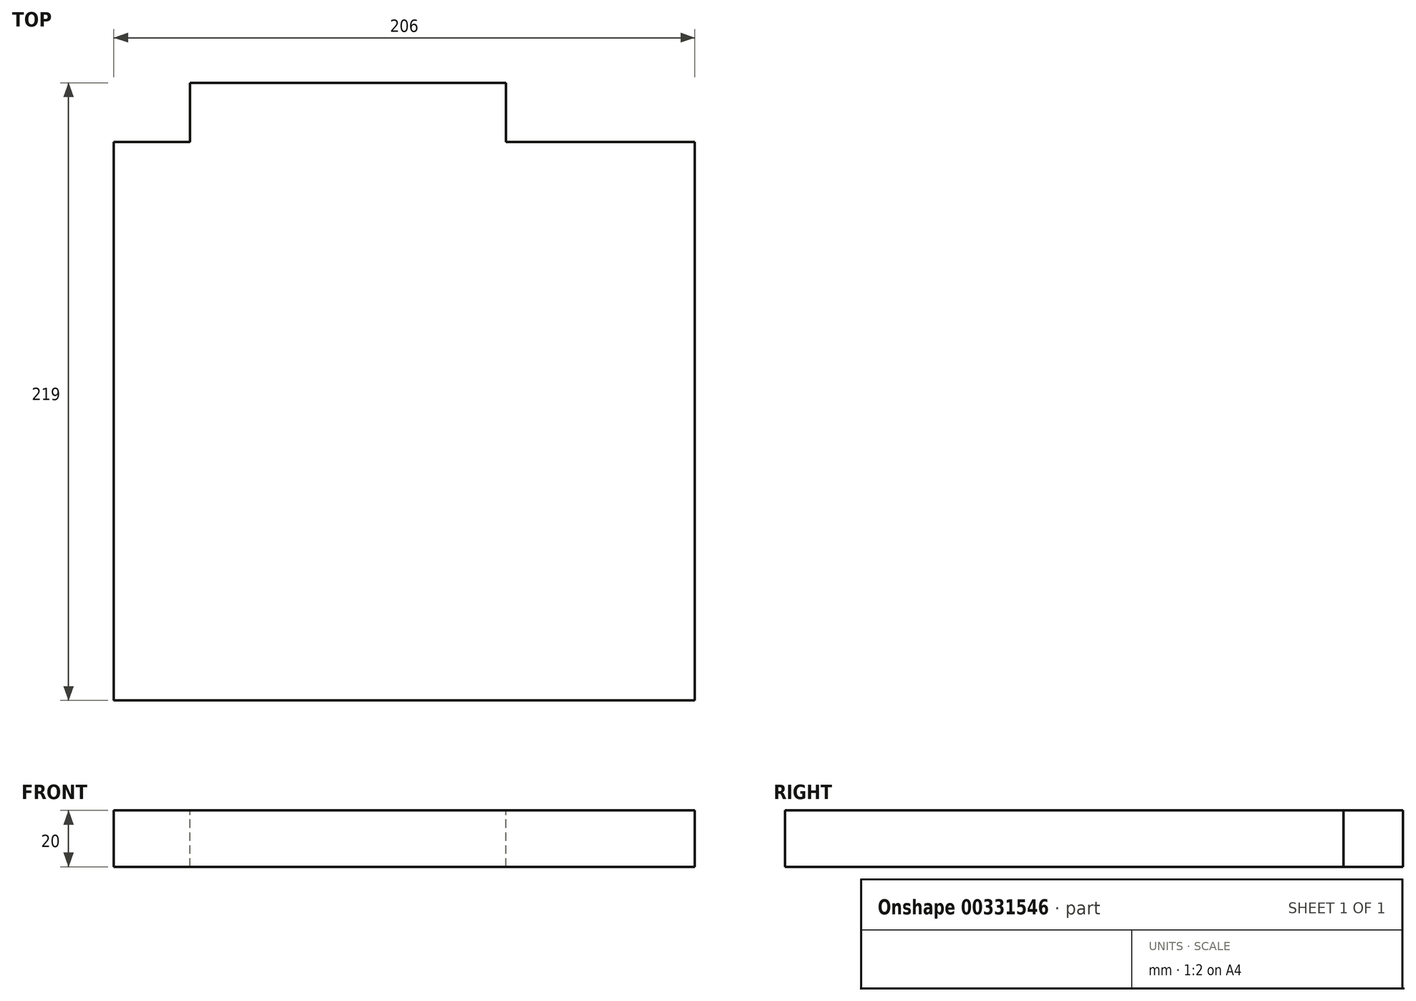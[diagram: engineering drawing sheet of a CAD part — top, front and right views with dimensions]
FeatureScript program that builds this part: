
annotation { "Feature Type Name" : "Feature", "Feature Type Description" : "" }
export const myFeature = defineFeature(function(context is Context, id is Id, definition is map)
    precondition{}
    {
        {
            var Q0;
            Q0=qCreatedBy(makeId("Top.planeOp"),FACE);
            var sketch = newSketch(context, id + "F0", { "sketchPlane" : qUnion([Q0])});
            skLineSegment(sketch, "E0", {"start": v(1313, 440) * mm, "end": v(1313, 406) * mm});
            skLineSegment(sketch, "E1", {"start": v(1313, -267) * mm, "end": v(1313, -301) * mm});
            skLineSegment(sketch, "E2", {"start": v(1313, -301) * mm, "end": v(647, -301) * mm});
            skLineSegment(sketch, "E3", {"start": v(1279, -267) * mm, "end": v(647, -267) * mm});
            skLineSegment(sketch, "E4", {"start": v(1279, 406) * mm, "end": v(688, 406) * mm});
            skLineSegment(sketch, "E5", {"start": v(688, 406) * mm, "end": v(688, -75) * mm});
            skLineSegment(sketch, "E6", {"start": v(688, -75) * mm, "end": v(413, -75) * mm});
            skLineSegment(sketch, "E7", {"start": v(647, -301) * mm, "end": v(647, -267) * mm});
            skLineSegment(sketch, "E8", {"start": v(536, -301) * mm, "end": v(536, -267) * mm});
            skLineSegment(sketch, "E9", {"start": v(536, -267) * mm, "end": v(328, -267) * mm});
            skLineSegment(sketch, "E10", {"start": v(328, -267) * mm, "end": v(328, -407) * mm});
            skLineSegment(sketch, "E11", {"start": v(328, -407) * mm, "end": v(-40, -407) * mm});
            skLineSegment(sketch, "E12", {"start": v(-40, -407) * mm, "end": v(-40, -188) * mm});
            skLineSegment(sketch, "E13", {"start": v(-40, -188) * mm, "end": v(-105, -188) * mm});
            skLineSegment(sketch, "E14", {"start": v(536, -301) * mm, "end": v(362, -301) * mm});
            skLineSegment(sketch, "E15", {"start": v(362, -301) * mm, "end": v(362, -440) * mm});
            skLineSegment(sketch, "E16", {"start": v(-60, -407) * mm, "end": v(-60, -215) * mm});
            skLineSegment(sketch, "E17", {"start": v(-60, -215) * mm, "end": v(-105, -215) * mm});
            skLineSegment(sketch, "E18", {"start": v(-105, -188) * mm, "end": v(-105, -215) * mm});
            skLineSegment(sketch, "E19", {"start": v(-60, -407) * mm, "end": v(-282, -407) * mm});
            skLineSegment(sketch, "E20", {"start": v(-282, -407) * mm, "end": v(-282, -287) * mm});
            skLineSegment(sketch, "E21", {"start": v(-282, -287) * mm, "end": v(-330, -287) * mm});
            skLineSegment(sketch, "E22", {"start": v(-330, -287) * mm, "end": v(-330, -407) * mm});
            skLineSegment(sketch, "E23", {"start": v(-330, -407) * mm, "end": v(-497, -407) * mm});
            skLineSegment(sketch, "E24", {"start": v(-197, -188) * mm, "end": v(-197, -215) * mm});
            skLineSegment(sketch, "E25", {"start": v(-197, -188) * mm, "end": v(-765, -188) * mm});
            skLineSegment(sketch, "E26", {"start": v(-197, -215) * mm, "end": v(-497, -215) * mm});
            skLineSegment(sketch, "E27", {"start": v(-497, -215) * mm, "end": v(-497, -231) * mm});
            skLineSegment(sketch, "E28", {"start": v(-497, -231) * mm, "end": v(-497, -293) * mm});
            skLineSegment(sketch, "E29", {"start": v(-497, -407) * mm, "end": v(-497, -349) * mm});
            skLineSegment(sketch, "E30", {"start": v(413, -75) * mm, "end": v(413, -54) * mm});
            skLineSegment(sketch, "E31", {"start": v(413, -54) * mm, "end": v(667, -54) * mm});
            skLineSegment(sketch, "E32", {"start": v(667, -54) * mm, "end": v(667, 406) * mm});
            skLineSegment(sketch, "E33", {"start": v(667, 406) * mm, "end": v(495, 406) * mm});
            skLineSegment(sketch, "E34", {"start": v(312, 406) * mm, "end": v(391, 406) * mm});
            skLineSegment(sketch, "E35", {"start": v(391, 406) * mm, "end": v(391, 440) * mm});
            skLineSegment(sketch, "E36", {"start": v(495, 406) * mm, "end": v(495, 440) * mm});
            skLineSegment(sketch, "E37", {"start": v(1313, 440) * mm, "end": v(495, 440) * mm});
            skLineSegment(sketch, "E38", {"start": v(312, -75) * mm, "end": v(60, -75) * mm});
            skLineSegment(sketch, "E39", {"start": v(-1279, 406) * mm, "end": v(-1279, 7) * mm});
            skLineSegment(sketch, "E40", {"start": v(-790, 406) * mm, "end": v(-790, 7) * mm});
            skLineSegment(sketch, "E41", {"start": v(-1279, 7) * mm, "end": v(-910, 7) * mm});
            skLineSegment(sketch, "E42", {"start": v(-790, 7) * mm, "end": v(-808, 7) * mm});
            skLineSegment(sketch, "E43", {"start": v(-765, -188) * mm, "end": v(-765, -208) * mm});
            skLineSegment(sketch, "E44", {"start": v(290, 141) * mm, "end": v(290, 406) * mm});
            skLineSegment(sketch, "E45", {"start": v(290, 141) * mm, "end": v(75, 141) * mm});
            skLineSegment(sketch, "E46", {"start": v(75, -46) * mm, "end": v(75, 141) * mm});
            skLineSegment(sketch, "E47", {"start": v(60, -75) * mm, "end": v(60, -46) * mm});
            skLineSegment(sketch, "E48", {"start": v(391, 406) * mm, "end": v(312, 406) * mm});
            skLineSegment(sketch, "E49", {"start": v(-139, 406) * mm, "end": v(-139, 440) * mm});
            skLineSegment(sketch, "E50", {"start": v(-318, 406) * mm, "end": v(-318, 440) * mm});
            skLineSegment(sketch, "E51", {"start": v(-515, 406) * mm, "end": v(-515, 440) * mm});
            skLineSegment(sketch, "E52", {"start": v(-694, 406) * mm, "end": v(-694, 440) * mm});
            skLineSegment(sketch, "E53", {"start": v(-770, 406) * mm, "end": v(-770, 9) * mm});
            skLineSegment(sketch, "E54", {"start": v(-694, 406) * mm, "end": v(-770, 406) * mm});
            skLineSegment(sketch, "E55", {"start": v(75, 406) * mm, "end": v(-139, 406) * mm});
            skLineSegment(sketch, "E56", {"start": v(-318, 406) * mm, "end": v(-515, 406) * mm});
            skLineSegment(sketch, "E57", {"start": v(-318, 440) * mm, "end": v(-515, 440) * mm});
            skLineSegment(sketch, "E58", {"start": v(-770, 9) * mm, "end": v(-754, 9) * mm});
            skLineSegment(sketch, "E59", {"start": v(-677, 9) * mm, "end": v(-659, 9) * mm});
            skLineSegment(sketch, "E60", {"start": v(-659, 9) * mm, "end": v(-659, -5) * mm});
            skLineSegment(sketch, "E61", {"start": v(-659, -5) * mm, "end": v(-659, -46) * mm});
            skLineSegment(sketch, "E62", {"start": v(-659, -46) * mm, "end": v(-60, -46) * mm});
            skLineSegment(sketch, "E63", {"start": v(-60, -75) * mm, "end": v(-60, -46) * mm});
            skLineSegment(sketch, "E64", {"start": v(60, -75) * mm, "end": v(128, -75) * mm});
            skLineSegment(sketch, "E65", {"start": v(60, -46) * mm, "end": v(75, -46) * mm});
            skLineSegment(sketch, "E66", {"start": v(96, -46) * mm, "end": v(290, -46) * mm});
            skLineSegment(sketch, "E67", {"start": v(-60, -75) * mm, "end": v(-677, -75) * mm});
            skLineSegment(sketch, "E68", {"start": v(-677, 9) * mm, "end": v(-677, -75) * mm});
            skLineSegment(sketch, "E69", {"start": v(-754, 9) * mm, "end": v(-754, -13) * mm});
            skLineSegment(sketch, "E70", {"start": v(-808, 7) * mm, "end": v(-808, -13) * mm});
            skLineSegment(sketch, "E71", {"start": v(-808, -13) * mm, "end": v(-754, -13) * mm});
            skLineSegment(sketch, "E72", {"start": v(-910, 7) * mm, "end": v(-910, -29) * mm});
            skLineSegment(sketch, "E73", {"start": v(-1279, -406) * mm, "end": v(-935, -406) * mm});
            skLineSegment(sketch, "E74", {"start": v(-1313, -440) * mm, "end": v(-935, -440) * mm});
            skLineSegment(sketch, "E75", {"start": v(-910, -29) * mm, "end": v(-935, -29) * mm});
            skLineSegment(sketch, "E76", {"start": v(-935, -13) * mm, "end": v(-1279, -13) * mm});
            skLineSegment(sketch, "E77", {"start": v(-910, -132) * mm, "end": v(-935, -132) * mm});
            skLineSegment(sketch, "E78", {"start": v(-910, -29) * mm, "end": v(-910, -13) * mm});
            skLineSegment(sketch, "E79", {"start": v(-935, -406) * mm, "end": v(-935, -132) * mm});
            skLineSegment(sketch, "E80", {"start": v(-935, -29) * mm, "end": v(-935, -13) * mm});
            skLineSegment(sketch, "E81", {"start": v(-877, -208) * mm, "end": v(-877, -188) * mm});
            skLineSegment(sketch, "E82", {"start": v(-910, -132) * mm, "end": v(-910, -188) * mm});
            skLineSegment(sketch, "E83", {"start": v(-877, -188) * mm, "end": v(-910, -188) * mm});
            skLineSegment(sketch, "E84", {"start": v(-877, -208) * mm, "end": v(-904, -208) * mm});
            skLineSegment(sketch, "E85", {"start": v(-904, -208) * mm, "end": v(-904, -406) * mm});
            skLineSegment(sketch, "E86", {"start": v(-904, -406) * mm, "end": v(-648, -406) * mm});
            skLineSegment(sketch, "E87", {"start": v(-765, -208) * mm, "end": v(-648, -208) * mm});
            skLineSegment(sketch, "E88", {"start": v(-648, -208) * mm, "end": v(-648, -273) * mm});
            skLineSegment(sketch, "E89", {"start": v(-648, -406) * mm, "end": v(-648, -343) * mm});
            skLineSegment(sketch, "E90", {"start": v(-935, -440) * mm, "end": v(362, -440) * mm});
            skLineSegment(sketch, "E91", {"start": v(151, 406) * mm, "end": v(151, 440) * mm});
            skLineSegment(sketch, "E92", {"start": v(224, 406) * mm, "end": v(224, 440) * mm});
            skLineSegment(sketch, "E93", {"start": v(290, 406) * mm, "end": v(224, 406) * mm});
            skLineSegment(sketch, "E94", {"start": v(151, 406) * mm, "end": v(96, 406) * mm});
            skLineSegment(sketch, "E95", {"start": v(391, 440) * mm, "end": v(224, 440) * mm});
            skLineSegment(sketch, "E96", {"start": v(151, 440) * mm, "end": v(-139, 440) * mm});
            skLineSegment(sketch, "E97", {"start": v(-907, 406) * mm, "end": v(-907, 440) * mm});
            skLineSegment(sketch, "E98", {"start": v(-1085, 406) * mm, "end": v(-1085, 440) * mm});
            skLineSegment(sketch, "E99", {"start": v(-790, 406) * mm, "end": v(-907, 406) * mm});
            skLineSegment(sketch, "E100", {"start": v(-1085, 406) * mm, "end": v(-1279, 406) * mm});
            skLineSegment(sketch, "E101", {"start": v(-694, 440) * mm, "end": v(-907, 440) * mm});
            skLineSegment(sketch, "E102", {"start": v(-1085, 440) * mm, "end": v(-1313, 440) * mm});
            skLineSegment(sketch, "E103", {"start": v(-1279, -118) * mm, "end": v(-1313, -118) * mm});
            skLineSegment(sketch, "E104", {"start": v(-1279, -297) * mm, "end": v(-1313, -297) * mm});
            skLineSegment(sketch, "E105", {"start": v(-1279, -13) * mm, "end": v(-1279, -118) * mm});
            skLineSegment(sketch, "E106", {"start": v(-1279, -297) * mm, "end": v(-1279, -406) * mm});
            skLineSegment(sketch, "E107", {"start": v(-1313, 440) * mm, "end": v(-1313, -118) * mm});
            skLineSegment(sketch, "E108", {"start": v(-1313, -297) * mm, "end": v(-1313, -440) * mm});
            skLineSegment(sketch, "E109", {"start": v(-648, -273) * mm, "end": v(-630, -273) * mm});
            skLineSegment(sketch, "E110", {"start": v(-648, -343) * mm, "end": v(-630, -343) * mm});
            skLineSegment(sketch, "E111", {"start": v(-515, -349) * mm, "end": v(-497, -349) * mm});
            skLineSegment(sketch, "E112", {"start": v(-515, -293) * mm, "end": v(-497, -293) * mm});
            skLineSegment(sketch, "E113", {"start": v(-515, -349) * mm, "end": v(-515, -406) * mm});
            skLineSegment(sketch, "E114", {"start": v(-630, -343) * mm, "end": v(-630, -406) * mm});
            skLineSegment(sketch, "E115", {"start": v(-630, -406) * mm, "end": v(-515, -406) * mm});
            skLineSegment(sketch, "E116", {"start": v(-630, -273) * mm, "end": v(-630, -206) * mm});
            skLineSegment(sketch, "E117", {"start": v(-630, -206) * mm, "end": v(-515, -206) * mm});
            skLineSegment(sketch, "E118", {"start": v(-515, -293) * mm, "end": v(-515, -206) * mm});
            skLineSegment(sketch, "E119", {"start": v(290, 43) * mm, "end": v(312, 43) * mm});
            skLineSegment(sketch, "E120", {"start": v(290, 124) * mm, "end": v(312, 124) * mm});
            skLineSegment(sketch, "E121", {"start": v(312, -75) * mm, "end": v(312, 43) * mm});
            skLineSegment(sketch, "E122", {"start": v(312, 124) * mm, "end": v(312, 406) * mm});
            skLineSegment(sketch, "E123", {"start": v(290, -46) * mm, "end": v(290, 43) * mm});
            skLineSegment(sketch, "E124", {"start": v(96, 222) * mm, "end": v(75, 222) * mm});
            skLineSegment(sketch, "E125", {"start": v(96, 222) * mm, "end": v(96, 406) * mm});
            skLineSegment(sketch, "E126", {"start": v(75, 222) * mm, "end": v(75, 406) * mm});
            skLineSegment(sketch, "E127", {"start": v(96, -46) * mm, "end": v(96, 124) * mm});
            skLineSegment(sketch, "E128", {"start": v(290, 124) * mm, "end": v(96, 124) * mm});
            skLineSegment(sketch, "E129", {"start": v(1279, -219) * mm, "end": v(1313, -219) * mm});
            skLineSegment(sketch, "E130", {"start": v(1279, -26) * mm, "end": v(1313, -26) * mm});
            skLineSegment(sketch, "E131", {"start": v(1279, 46) * mm, "end": v(1313, 46) * mm});
            skLineSegment(sketch, "E132", {"start": v(1279, 239) * mm, "end": v(1313, 239) * mm});
            skLineSegment(sketch, "E133", {"start": v(1313, 406) * mm, "end": v(1313, 239) * mm});
            skLineSegment(sketch, "E134", {"start": v(1279, 406) * mm, "end": v(1279, 239) * mm});
            skLineSegment(sketch, "E135", {"start": v(1313, 46) * mm, "end": v(1313, -26) * mm});
            skLineSegment(sketch, "E136", {"start": v(1313, -219) * mm, "end": v(1313, -267) * mm});
            skLineSegment(sketch, "E137", {"start": v(1279, 46) * mm, "end": v(1279, -26) * mm});
            skLineSegment(sketch, "E138", {"start": v(1279, -219) * mm, "end": v(1279, -267) * mm});
            skLineSegment(sketch, "E139", {"start": v(1313, -301) * mm, "end": v(1313, 440) * mm});
            skLineSegment(sketch, "E140", {"start": v(1313, -301) * mm, "end": v(362, -301) * mm});
            skLineSegment(sketch, "E141", {"start": v(362, -440) * mm, "end": v(-1313, -440) * mm});
            skLineSegment(sketch, "E142", {"start": v(-1313, 440) * mm, "end": v(-1313, -440) * mm});
            skLineSegment(sketch, "E143", {"start": v(-1313, 440) * mm, "end": v(1313, 440) * mm});
            skLineSegment(sketch, "E144", {"start": v(-321.5, -37.21) * mm, "end": v(-321.5, 162.79) * mm});
            skLineSegment(sketch, "E145", {"start": v(-321.5, -37.21) * mm, "end": v(-511.5, -37.21) * mm});
            skLineSegment(sketch, "E146", {"start": v(-321.5, 162.79) * mm, "end": v(-511.5, 162.79) * mm});
            skLineSegment(sketch, "E147", {"start": v(-511.5, -37.21) * mm, "end": v(-511.5, 162.79) * mm});
            skLineSegment(sketch, "E148", {"start": v(-321.5, -29.2) * mm, "end": v(-511.5, -29.2) * mm});
            skLineSegment(sketch, "E149", {"start": v(-499.08, -21.75) * mm, "end": v(-430.85, -21.75) * mm});
            skLineSegment(sketch, "E150", {"start": v(-430.85, -21.75) * mm, "end": v(-430.85, 2.94) * mm});
            skLineSegment(sketch, "E151", {"start": v(-430.85, 2.94) * mm, "end": v(-499.08, 2.94) * mm});
            skLineSegment(sketch, "E152", {"start": v(-499.08, 2.94) * mm, "end": v(-499.08, -21.75) * mm});
            skLineSegment(sketch, "E153", {"start": v(-333.92, -21.75) * mm, "end": v(-402.15, -21.75) * mm});
            skLineSegment(sketch, "E154", {"start": v(-402.15, -21.75) * mm, "end": v(-402.15, 2.94) * mm});
            skLineSegment(sketch, "E155", {"start": v(-402.15, 2.94) * mm, "end": v(-333.92, 2.94) * mm});
            skLineSegment(sketch, "E156", {"start": v(-333.92, 2.94) * mm, "end": v(-333.92, -21.75) * mm});
            skLineSegment(sketch, "E157", {"start": v(-321.5, 13.1) * mm, "end": v(-416.5, 13.1) * mm});
            skLineSegment(sketch, "E158", {"start": v(-511.5, 36.6) * mm, "end": v(-491.94, 63.04) * mm});
            skLineSegment(sketch, "E159", {"start": v(-491.94, 63.04) * mm, "end": v(-416.5, 13.1) * mm});
            skLineSegment(sketch, "E160", {"start": v(-416.5, 13.1) * mm, "end": v(-511.5, 36.6) * mm});
            skLineSegment(sketch, "E161", {"start": v(-321.5, 159.23) * mm, "end": v(-511.5, 159.23) * mm});
            skLineSegment(sketch, "E162", {"start": v(-552.43, 3.31) * mm, "end": v(-520.43, 3.31) * mm});
            skLineSegment(sketch, "E163", {"start": v(-552.43, 3.31) * mm, "end": v(-552.43, -36.7) * mm});
            skLineSegment(sketch, "E164", {"start": v(-520.43, 3.31) * mm, "end": v(-520.43, -36.7) * mm});
            skLineSegment(sketch, "E165", {"start": v(-552.43, -36.7) * mm, "end": v(-520.43, -36.7) * mm});
            skLineSegment(sketch, "E166", {"start": v(-552.43, -6.69) * mm, "end": v(-520.43, -6.69) * mm});
            skLineSegment(sketch, "E167", {"start": v(-552.43, -3.69) * mm, "end": v(-520.43, -3.69) * mm});
            skLineSegment(sketch, "E168", {"start": v(-552.43, -0.69) * mm, "end": v(-520.43, -0.69) * mm});
            skLineSegment(sketch, "E169", {"start": v(-552.43, 2.31) * mm, "end": v(-520.43, 2.31) * mm});
            skLineSegment(sketch, "E170", {"start": v(-280.57, 3.31) * mm, "end": v(-312.57, 3.31) * mm});
            skLineSegment(sketch, "E171", {"start": v(-280.57, 3.31) * mm, "end": v(-280.57, -36.7) * mm});
            skLineSegment(sketch, "E172", {"start": v(-312.57, 3.31) * mm, "end": v(-312.57, -36.7) * mm});
            skLineSegment(sketch, "E173", {"start": v(-280.57, -36.7) * mm, "end": v(-312.57, -36.7) * mm});
            skLineSegment(sketch, "E174", {"start": v(-280.57, -6.69) * mm, "end": v(-312.57, -6.69) * mm});
            skLineSegment(sketch, "E175", {"start": v(-280.57, -3.69) * mm, "end": v(-312.57, -3.69) * mm});
            skLineSegment(sketch, "E176", {"start": v(-280.57, -0.69) * mm, "end": v(-312.57, -0.69) * mm});
            skLineSegment(sketch, "E177", {"start": v(-280.57, 2.31) * mm, "end": v(-312.57, 2.31) * mm});
            skLineSegment(sketch, "E178", {"start": v(-765, 395.6) * mm, "end": v(-765, 20.6) * mm});
            skLineSegment(sketch, "E179", {"start": v(-765, 395.6) * mm, "end": v(-705, 395.6) * mm});
            skLineSegment(sketch, "E180", {"start": v(-705, 395.6) * mm, "end": v(-705, 20.6) * mm});
            skLineSegment(sketch, "E181", {"start": v(-765, 20.6) * mm, "end": v(-705, 20.6) * mm});
            skLineSegment(sketch, "E182", {"start": v(-705, 395.6) * mm, "end": v(-700, 395.6) * mm});
            skLineSegment(sketch, "E183", {"start": v(-700, 395.6) * mm, "end": v(-700, 20.6) * mm});
            skLineSegment(sketch, "E184", {"start": v(-705, 20.6) * mm, "end": v(-700, 20.6) * mm});
            skLineSegment(sketch, "E185", {"start": v(-705, 114.35) * mm, "end": v(-700, 114.35) * mm});
            skLineSegment(sketch, "E186", {"start": v(-705, 301.85) * mm, "end": v(-700, 301.85) * mm});
            skLineSegment(sketch, "E187", {"start": v(-705, 208.1) * mm, "end": v(-700, 208.1) * mm});
            skLineSegment(sketch, "E188", {"start": v(-705, 348.73) * mm, "end": v(-700, 348.73) * mm});
            skLineSegment(sketch, "E189", {"start": v(-705, 67.47) * mm, "end": v(-700, 67.47) * mm});
            skSolve(sketch);
        }
        {
            var Q0;
            Q0=makeQuery(id+"F0.imprint","IMPRINT",FACE,{"disambiguationData":[TD([[makeQuery(id+"F0.imprint","IMPRINT",EDGE,{"derivedFrom":sQuery(id+"F0.wireOp",EDGE,"E3")}),-1.0]])]});
            var sketch = newSketch(context, id + "F1", { "sketchPlane" : qUnion([Q0])});
            skLineSegment(sketch, "E190.0", {"start": v(-904, -208) * mm, "end": v(-904, -406) * mm});
            skLineSegment(sketch, "E191.0", {"start": v(-904, -406) * mm, "end": v(-648, -406) * mm});
            skLineSegment(sketch, "E192.0", {"start": v(-648, -208) * mm, "end": v(-648, -273) * mm});
            skLineSegment(sketch, "E193.0", {"start": v(-648, -406) * mm, "end": v(-648, -343) * mm});
            skLineSegment(sketch, "E194.0", {"start": v(-765, -208) * mm, "end": v(-648, -208) * mm});
            skLineSegment(sketch, "E195", {"start": v(-648, -273) * mm, "end": v(-648, -343) * mm});
            skLineSegment(sketch, "E196", {"start": v(-765, -208) * mm, "end": v(-904, -208) * mm});
            skSolve(sketch);
        }
        {
            var Q0;
            {var subQ0=sQuery(id+"F1.wireOp",EDGE,"E190.0");Q0=makeQuery(id+"F1.imprint","IMPRINT",FACE,{"disambiguationData":[TD([[makeQuery(id+"F1.imprint","IMPRINT",EDGE,{"derivedFrom":subQ0}),1.0]])]});}
            var sketch = newSketch(context, id + "F2", { "sketchPlane" : qUnion([Q0])});
            skLineSegment(sketch, "E197.0", {"start": v(-627, -273) * mm, "end": v(-627, -187) * mm});
            skLineSegment(sketch, "E197.1", {"start": v(-627, -343) * mm, "end": v(-627, -273) * mm});
            skLineSegment(sketch, "E197.2", {"start": v(-627, -187) * mm, "end": v(-765, -187) * mm});
            skLineSegment(sketch, "E197.3", {"start": v(-627, -427) * mm, "end": v(-627, -343) * mm});
            skLineSegment(sketch, "E197.4", {"start": v(-765, -187) * mm, "end": v(-877, -187) * mm});
            skLineSegment(sketch, "E197.5", {"start": v(-877, -187) * mm, "end": v(-925, -187) * mm});
            skLineSegment(sketch, "E197.6", {"start": v(-925, -187) * mm, "end": v(-925, -427) * mm});
            skLineSegment(sketch, "E197.7", {"start": v(-925, -427) * mm, "end": v(-627, -427) * mm});
            skLineSegment(sketch, "E198.0.0", {"start": v(-648, -208) * mm, "end": v(-765, -208) * mm});
            skLineSegment(sketch, "E198.0.1", {"start": v(-765, -208) * mm, "end": v(-877, -208) * mm});
            skLineSegment(sketch, "E198.0.2", {"start": v(-877, -208) * mm, "end": v(-904, -208) * mm});
            skLineSegment(sketch, "E198.0.3", {"start": v(-904, -208) * mm, "end": v(-904, -406) * mm});
            skLineSegment(sketch, "E198.0.4", {"start": v(-904, -406) * mm, "end": v(-648, -406) * mm});
            skLineSegment(sketch, "E198.0.5", {"start": v(-648, -406) * mm, "end": v(-648, -343) * mm});
            skLineSegment(sketch, "E198.0.6", {"start": v(-648, -343) * mm, "end": v(-648, -273) * mm});
            skLineSegment(sketch, "E198.0.7", {"start": v(-648, -273) * mm, "end": v(-648, -208) * mm});
            skSolve(sketch);
        }
        {
            var Q0;
            Q0=qSketchRegion(id+"F2",true);
            extrude(context, id + "F3", {"entities" : qUnion([Q0]), "depth" : (220 + 20) * mm});
        }
        {
            var Q0;
            {var subQ0=sQuery(id+"F1.wireOp",EDGE,"E190.0");Q0=makeQuery(id+"F1.imprint","IMPRINT",FACE,{"disambiguationData":[TD([[makeQuery(id+"F1.imprint","IMPRINT",EDGE,{"derivedFrom":subQ0}),1.0]])]});}
            var sketch = newSketch(context, id + "F4", { "sketchPlane" : qUnion([Q0])});
            skLineSegment(sketch, "E199.0.0", {"start": v(-648, -208) * mm, "end": v(-765, -208) * mm});
            skLineSegment(sketch, "E199.0.1", {"start": v(-765, -208) * mm, "end": v(-877, -208) * mm});
            skLineSegment(sketch, "E199.0.2", {"start": v(-877, -208) * mm, "end": v(-904, -208) * mm});
            skLineSegment(sketch, "E199.0.3", {"start": v(-904, -208) * mm, "end": v(-904, -406) * mm});
            skLineSegment(sketch, "E199.0.4", {"start": v(-904, -406) * mm, "end": v(-648, -406) * mm});
            skLineSegment(sketch, "E199.0.5", {"start": v(-648, -406) * mm, "end": v(-648, -343) * mm});
            skLineSegment(sketch, "E199.0.6", {"start": v(-648, -343) * mm, "end": v(-648, -273) * mm});
            skLineSegment(sketch, "E199.0.7", {"start": v(-648, -273) * mm, "end": v(-648, -208) * mm});
            skSolve(sketch);
        }
        {
            var Q0;
            Q0=qSketchRegion(id+"F4",true);
            extrude(context, id + "F5", {"entities" : qUnion([Q0]), "operationType" : NewBodyOperationType.ADD, "depth" : 20 * mm});
        }
        {
            var Q0;
            Q0=makeQuery(id+"F3.opExtrude","SWEPT_FACE",FACE,{"disambiguationData":[OSD([sQuery(id+"F2.wireOp",EDGE,"E197.2"),sQuery(id+"F2.wireOp",EDGE,"E197.4"),sQuery(id+"F2.wireOp",EDGE,"E197.5")])]});
            var sketch = newSketch(context, id + "F6", { "sketchPlane" : qUnion([Q0])});
            skLineSegment(sketch, "E200.0", {"start": v(904, 240) * mm, "end": v(904, 20) * mm});
            skLineSegment(sketch, "E201.0", {"start": v(877, 0) * mm, "end": v(910, 0) * mm});
            skLineSegment(sketch, "E202.0", {"start": v(197, 0) * mm, "end": v(765, 0) * mm});
            skLineSegment(sketch, "E203", {"start": v(877, 20) * mm, "end": v(877, 261.1) * mm});
            skLineSegment(sketch, "E204", {"start": v(877, 261.1) * mm, "end": v(765, 261.1) * mm});
            skLineSegment(sketch, "E205", {"start": v(765, 261.1) * mm, "end": v(765, 20) * mm});
            skLineSegment(sketch, "E206", {"start": v(765, 20) * mm, "end": v(877, 20) * mm});
            skSolve(sketch);
        }
        {
            var Q0;
            Q0=qSketchRegion(id+"F6",true);
            extrude(context, id + "F7", {"entities" : qUnion([Q0]), "operationType" : NewBodyOperationType.REMOVE, "oppositeDirection" : true, "depth" : 25 * mm});
        }
        {
            var Q0;
            Q0=makeQuery(id+"F3.opExtrude","SWEPT_FACE",FACE,{"disambiguationData":[OSD([sQuery(id+"F2.wireOp",EDGE,"E197.0"),sQuery(id+"F2.wireOp",EDGE,"E197.1"),sQuery(id+"F2.wireOp",EDGE,"E197.3")])]});
            var sketch = newSketch(context, id + "F8", { "sketchPlane" : qUnion([Q0])});
            skLineSegment(sketch, "E207.0", {"start": v(-208, 0) * mm, "end": v(-273, 0) * mm, "construction": true});
            skLineSegment(sketch, "E208.0", {"start": v(-406, 0) * mm, "end": v(-343, 0) * mm, "construction": true});
            skLineSegment(sketch, "E209.0", {"start": v(-406, 20) * mm, "end": v(-208, 20) * mm, "construction": true});
            skLineSegment(sketch, "E210", {"start": v(-273, 135) * mm, "end": v(-343, 135) * mm});
            skLineSegment(sketch, "E211", {"start": v(-343, 135) * mm, "end": v(-343, 220) * mm});
            skLineSegment(sketch, "E212", {"start": v(-343, 220) * mm, "end": v(-273, 220) * mm});
            skLineSegment(sketch, "E213", {"start": v(-273, 220) * mm, "end": v(-273, 135) * mm});
            skSolve(sketch);
        }
        {
            var Q0;
            Q0=qSketchRegion(id+"F8",true);
            extrude(context, id + "F9", {"entities" : qUnion([Q0]), "operationType" : NewBodyOperationType.REMOVE, "oppositeDirection" : true, "depth" : 25 * mm});
        }
        {
            var Q0;
            Q0=makeQuery(id+"F7.boolean.opBoolean","MERGE",FACE,{"derivedFrom":[makeQuery(id+"F5.opExtrude","CAP_FACE",FACE,{"disambiguationData":[OSD([sQuery(id+"F4.wireOp",EDGE,"E199.0.0"),sQuery(id+"F4.wireOp",EDGE,"E199.0.1"),sQuery(id+"F4.wireOp",EDGE,"E199.0.2"),sQuery(id+"F4.wireOp",EDGE,"E199.0.3"),sQuery(id+"F4.wireOp",EDGE,"E199.0.4"),sQuery(id+"F4.wireOp",EDGE,"E199.0.5"),sQuery(id+"F4.wireOp",EDGE,"E199.0.6"),sQuery(id+"F4.wireOp",EDGE,"E199.0.7")])],"isStart":false}),makeQuery(id+"F7.opExtrude","SWEPT_FACE",FACE,{"disambiguationData":[OSD([sQuery(id+"F6.wireOp",EDGE,"E206")])]})]});
            var sketch = newSketch(context, id + "F10", { "sketchPlane" : qUnion([Q0])});
            skLineSegment(sketch, "E214.0", {"start": v(-648, -406) * mm, "end": v(-648, -208) * mm});
            skLineSegment(sketch, "E215", {"start": v(-648, -208) * mm, "end": v(-698, -208) * mm});
            skLineSegment(sketch, "E216", {"start": v(-698, -208) * mm, "end": v(-698, -406) * mm});
            skLineSegment(sketch, "E217", {"start": v(-698, -406) * mm, "end": v(-648, -406) * mm});
            skSolve(sketch);
        }
        {
            var Q0;
            Q0=qSketchRegion(id+"F10",true);
            extrude(context, id + "F11", {"entities" : qUnion([Q0]), "operationType" : NewBodyOperationType.ADD, "depth" : 50 * mm});
        }
        {
            var Q0;
            Q0=makeQuery(id+"F3.opExtrude","CAP_FACE",FACE,{"disambiguationData":[OSD([sQuery(id+"F2.wireOp",EDGE,"E197.0"),sQuery(id+"F2.wireOp",EDGE,"E197.1"),sQuery(id+"F2.wireOp",EDGE,"E197.2"),sQuery(id+"F2.wireOp",EDGE,"E197.3"),sQuery(id+"F2.wireOp",EDGE,"E197.4"),sQuery(id+"F2.wireOp",EDGE,"E197.5"),sQuery(id+"F2.wireOp",EDGE,"E197.6"),sQuery(id+"F2.wireOp",EDGE,"E197.7"),sQuery(id+"F2.wireOp",EDGE,"E198.0.0"),sQuery(id+"F2.wireOp",EDGE,"E198.0.1"),sQuery(id+"F2.wireOp",EDGE,"E198.0.2"),sQuery(id+"F2.wireOp",EDGE,"E198.0.3"),sQuery(id+"F2.wireOp",EDGE,"E198.0.4"),sQuery(id+"F2.wireOp",EDGE,"E198.0.5"),sQuery(id+"F2.wireOp",EDGE,"E198.0.6"),sQuery(id+"F2.wireOp",EDGE,"E198.0.7")])],"isStart":false});
            extrude(context, id + "F12", {"entities" : qUnion([Q0]), "operationType" : NewBodyOperationType.REMOVE, "endBound" : BoundingType.THROUGH_ALL, "oppositeDirection" : true, "depth" : 25 * mm});
        }
        {
            var Q0;
            Q0=makeQuery(id+"F11.opExtrude","CAP_FACE",FACE,{"disambiguationData":[OSD([sQuery(id+"F10.wireOp",EDGE,"E214.0"),sQuery(id+"F10.wireOp",EDGE,"E215"),sQuery(id+"F10.wireOp",EDGE,"E216"),sQuery(id+"F10.wireOp",EDGE,"E217")])],"isStart":false});
            extrude(context, id + "F13", {"entities" : qUnion([Q0]), "operationType" : NewBodyOperationType.REMOVE, "endBound" : BoundingType.THROUGH_ALL, "oppositeDirection" : true, "depth" : 25 * mm});
        }
    });
